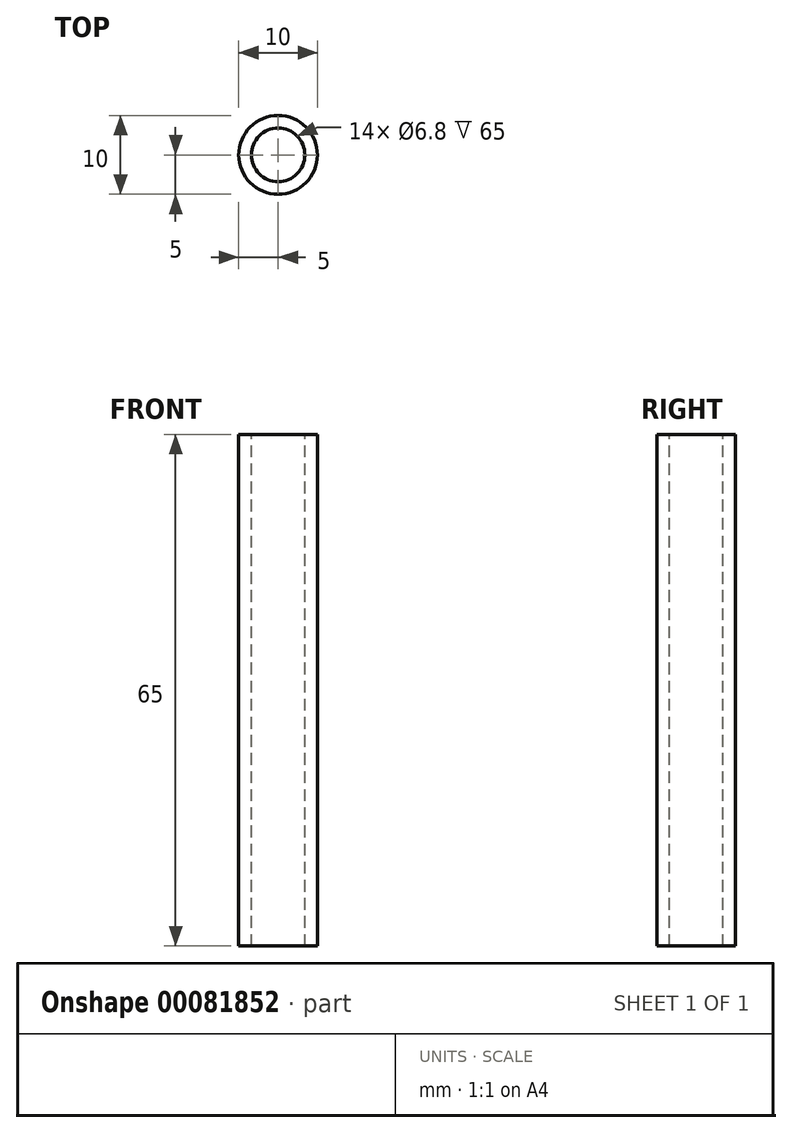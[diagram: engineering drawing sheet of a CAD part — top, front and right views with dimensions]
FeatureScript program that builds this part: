
annotation { "Feature Type Name" : "Feature", "Feature Type Description" : "" }
export const myFeature = defineFeature(function(context is Context, id is Id, definition is map)
    precondition{}
    {
        {
            var Q0;
            Q0=qCreatedBy(makeId("Top.planeOp"),FACE);
            var sketch = newSketch(context, id + "F0", { "sketchPlane" : qUnion([Q0])});
            skCircle(sketch, "E0", {"center": v(0, 0) * mm, "radius": 5 * mm});
            skCircle(sketch, "E1.0", {"center": v(0, 0) * mm, "radius": 3.4 * mm});
            skSolve(sketch);
        }
        {
            var Q0;
            Q0 = qSketchRegion(id + "F0", true);
            extrude(context, id + "F1", {"entities" : qUnion([Q0]), "oppositeDirection" : true, "depth" : 65 * mm});
        }
    });
